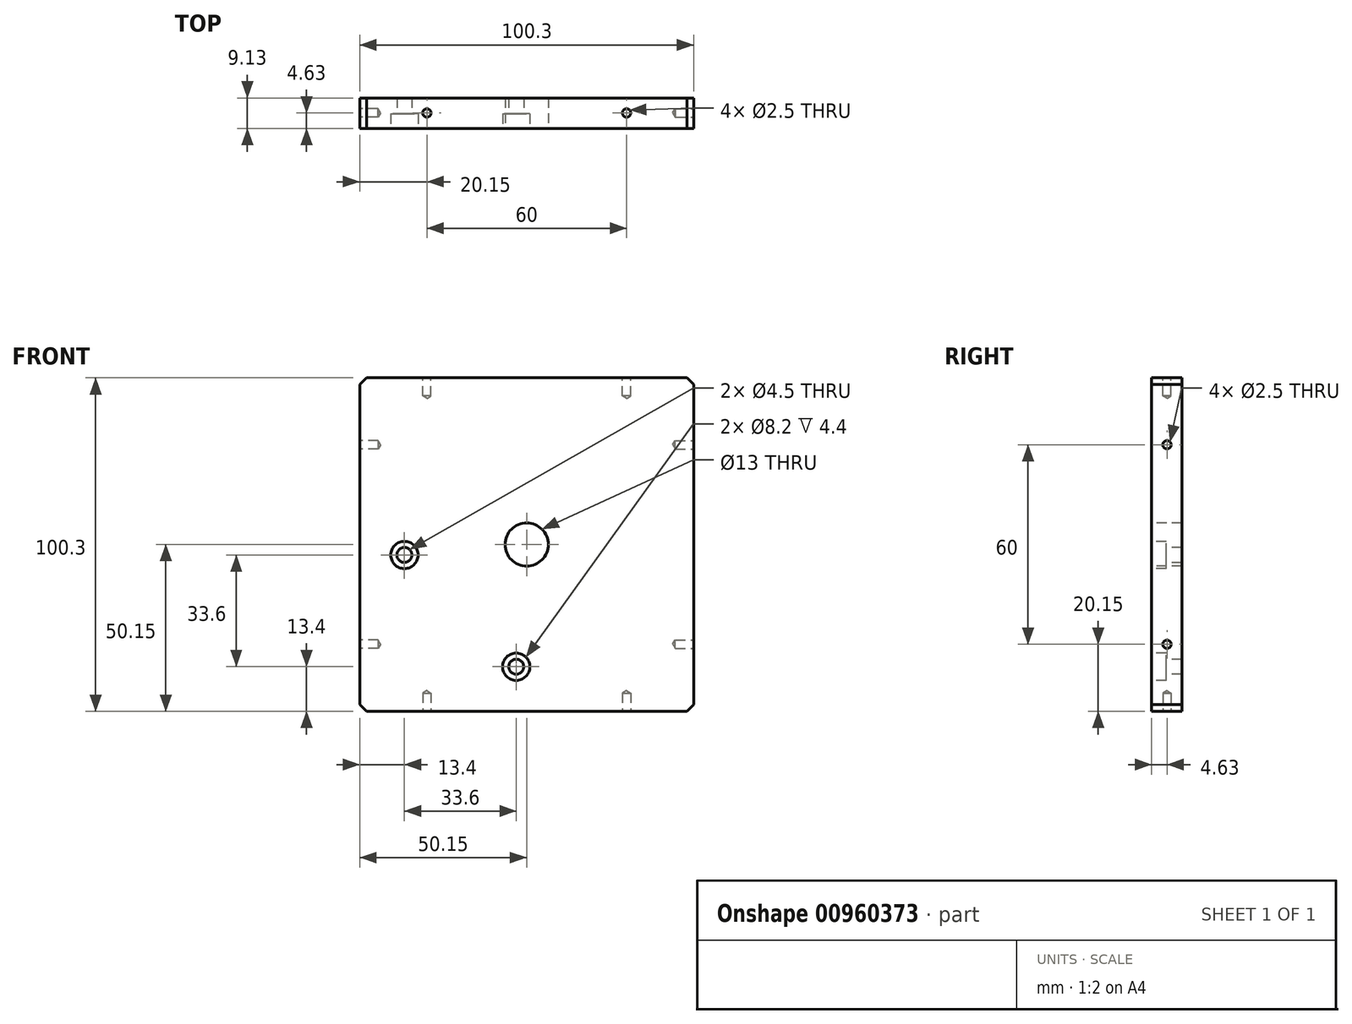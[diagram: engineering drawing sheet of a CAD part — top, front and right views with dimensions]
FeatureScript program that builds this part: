
annotation { "Feature Type Name" : "Feature", "Feature Type Description" : "" }
export const myFeature = defineFeature(function(context is Context, id is Id, definition is map)
    precondition{}
    {
        {
            var Q0;
            Q0=qCreatedBy(makeId("Front.planeOp"),FACE);
            var sketch = newSketch(context, id + "F0", { "sketchPlane" : qUnion([Q0])});
            skLineSegment(sketch, "E0.bottom", {"start": v(50.15, -50.15) * mm, "end": v(-50.15, -50.15) * mm});
            skLineSegment(sketch, "E0.top", {"start": v(50.15, 50.15) * mm, "end": v(-50.15, 50.15) * mm});
            skLineSegment(sketch, "E0.left", {"start": v(50.15, -50.15) * mm, "end": v(50.15, 50.15) * mm});
            skLineSegment(sketch, "E0.right", {"start": v(-50.15, -50.15) * mm, "end": v(-50.15, 50.15) * mm});
            skPoint(sketch, "E0.middle", {"position": v(0, 0) * mm});
            skPoint(sketch, "E1", {"position": v(-37.15, -3.15) * mm});
            skPoint(sketch, "E2", {"position": v(-3.15, -36.75) * mm});
            skSolve(sketch);
        }
        {
            var Q0;
            Q0=makeQuery(id+"F0.imprint","IMPRINT",FACE,{"disambiguationData":[TD([[makeQuery(id+"F0.imprint","IMPRINT",EDGE,{"derivedFrom":sQuery(id+"F0.wireOp",EDGE,"E0.bottom")}),-1.0]])]});
            extrude(context, id + "F1", {"entities" : qUnion([Q0]), "depth" : 9.13 * mm, "offsetDistance" : 25 * mm});
        }
        {
            var Q0;
            Q0=makeQuery(id+"F1.opExtrude","SWEPT_EDGE",EDGE,{"disambiguationData":[OSD([sQuery(id+"F0.wireOp",EDGE,"E0.bottom"),sQuery(id+"F0.wireOp",EDGE,"E0.right")])]});
            var Q1;
            Q1=makeQuery(id+"F1.opExtrude","SWEPT_EDGE",EDGE,{"disambiguationData":[OSD([sQuery(id+"F0.wireOp",EDGE,"E0.bottom"),sQuery(id+"F0.wireOp",EDGE,"E0.left")])]});
            var Q2;
            Q2=makeQuery(id+"F1.opExtrude","SWEPT_EDGE",EDGE,{"disambiguationData":[OSD([sQuery(id+"F0.wireOp",EDGE,"E0.top"),sQuery(id+"F0.wireOp",EDGE,"E0.left")])]});
            var Q3;
            Q3=makeQuery(id+"F1.opExtrude","SWEPT_EDGE",EDGE,{"disambiguationData":[OSD([sQuery(id+"F0.wireOp",EDGE,"E0.top"),sQuery(id+"F0.wireOp",EDGE,"E0.right")])]});
            chamfer(context, id + "F2", {"entities" : qUnion([Q0, Q1, Q2, Q3]), "width" : 2 * mm, "tangentPropagation" : true});
        }
        {
            var Q0;
            Q0=makeQuery(id+"F1.opExtrude","CAP_FACE",FACE,{"disambiguationData":[OSD([sQuery(id+"F0.wireOp",EDGE,"E0.bottom"),sQuery(id+"F0.wireOp",EDGE,"E0.top"),sQuery(id+"F0.wireOp",EDGE,"E0.left"),sQuery(id+"F0.wireOp",EDGE,"E0.right")])],"isStart":false});
            var sketch = newSketch(context, id + "F3", { "sketchPlane" : qUnion([Q0])});
            skPoint(sketch, "E3", {"position": v(-36.75, -3.15) * mm});
            skPoint(sketch, "E4", {"position": v(-3.15, -36.75) * mm});
            skPoint(sketch, "E5", {"position": v(0, 0) * mm});
            skSolve(sketch);
        }
        {
            var Q0;
            Q0=sQuery(id+"F3.wireOp",VERTEX,"E3");
            var Q1;
            Q1=sQuery(id+"F3.wireOp",VERTEX,"E4");
            var Q2;
            Q2=makeQuery(id+"F1.opExtrude","SWEPT_BODY",BODY,{"disambiguationData":[OSD([sQuery(id+"F0.wireOp",EDGE,"E0.bottom"),sQuery(id+"F0.wireOp",EDGE,"E0.top"),sQuery(id+"F0.wireOp",EDGE,"E0.left"),sQuery(id+"F0.wireOp",EDGE,"E0.right")])]});
            hole(context, id + "F4", {"style" : HoleStyle.C_BORE, "endStyle" : HoleEndStyle.THROUGH, "standardTappedOrClearance" : lookupTablePath({ "standard" : "ISO", "size" : "4.5", "type" : "Drilled" }), "standardBlindInLast" : lookupTablePath({ "standard" : "ISO", "size" : "4.5", "type" : "Drilled" }), "holeDiameter" : 4.5 * mm, "cBoreDiameter" : 8.2 * mm, "cBoreDepth" : 4.4 * mm, "majorDiameter" : 5 * mm, "isTappedThrough" : true, "tappedDepth" : 6 * mm, "tapClearance" : 3, "locations" : qUnion([Q0, Q1]), "scope" : qUnion([Q2])});
        }
        {
            var Q0;
            Q0=sQuery(id+"F3.wireOp",VERTEX,"E5");
            var Q1;
            Q1=makeQuery(id+"F1.opExtrude","SWEPT_BODY",BODY,{"disambiguationData":[OSD([sQuery(id+"F0.wireOp",EDGE,"E0.bottom"),sQuery(id+"F0.wireOp",EDGE,"E0.top"),sQuery(id+"F0.wireOp",EDGE,"E0.left"),sQuery(id+"F0.wireOp",EDGE,"E0.right")])]});
            hole(context, id + "F5", {"style" : HoleStyle.SIMPLE, "endStyle" : HoleEndStyle.THROUGH, "standardTappedOrClearance" : lookupTablePath({ "standard" : "ISO", "size" : "13", "type" : "Drilled" }), "standardBlindInLast" : lookupTablePath({ "standard" : "ISO", "size" : "13", "type" : "Drilled" }), "holeDiameter" : 13 * mm, "majorDiameter" : 5 * mm, "isTappedThrough" : true, "tappedDepth" : 6 * mm, "tapClearance" : 3, "locations" : qUnion([Q0]), "scope" : qUnion([Q1])});
        }
        {
            var Q0;
            Q0=makeQuery(id+"F1.opExtrude","SWEPT_FACE",FACE,{"disambiguationData":[OSD([sQuery(id+"F0.wireOp",EDGE,"E0.left")])]});
            var sketch = newSketch(context, id + "F6", { "sketchPlane" : qUnion([Q0])});
            skPoint(sketch, "E6", {"position": v(-4.5, -30) * mm});
            skPoint(sketch, "E7", {"position": v(-4.5, 30) * mm});
            skSolve(sketch);
        }
        {
            var Q0;
            Q0=makeQuery(id+"F1.opExtrude","SWEPT_FACE",FACE,{"disambiguationData":[OSD([sQuery(id+"F0.wireOp",EDGE,"E0.top")])]});
            var sketch = newSketch(context, id + "F7", { "sketchPlane" : qUnion([Q0])});
            skPoint(sketch, "E8", {"position": v(30, -4.5) * mm});
            skPoint(sketch, "E9", {"position": v(-30, -4.5) * mm});
            skSolve(sketch);
        }
        {
            var Q0;
            Q0=makeQuery(id+"F1.opExtrude","SWEPT_FACE",FACE,{"disambiguationData":[OSD([sQuery(id+"F0.wireOp",EDGE,"E0.right")])]});
            var sketch = newSketch(context, id + "F8", { "sketchPlane" : qUnion([Q0])});
            skPoint(sketch, "E10", {"position": v(4.5, 30) * mm});
            skPoint(sketch, "E11", {"position": v(4.5, -30) * mm});
            skSolve(sketch);
        }
        {
            var Q0;
            Q0=makeQuery(id+"F1.opExtrude","SWEPT_FACE",FACE,{"disambiguationData":[OSD([sQuery(id+"F0.wireOp",EDGE,"E0.bottom")])]});
            var sketch = newSketch(context, id + "F9", { "sketchPlane" : qUnion([Q0])});
            skPoint(sketch, "E12", {"position": v(-30, 4.5) * mm});
            skPoint(sketch, "E13", {"position": v(30, 4.5) * mm});
            skSolve(sketch);
        }
        {
            var Q0;
            Q0=sQuery(id+"F8.wireOp",VERTEX,"E11");
            var Q1;
            Q1=sQuery(id+"F8.wireOp",VERTEX,"E10");
            var Q2;
            Q2=sQuery(id+"F7.wireOp",VERTEX,"E9");
            var Q3;
            Q3=sQuery(id+"F7.wireOp",VERTEX,"E8");
            var Q4;
            Q4=sQuery(id+"F6.wireOp",VERTEX,"E6");
            var Q5;
            Q5=sQuery(id+"F6.wireOp",VERTEX,"E7");
            var Q6;
            Q6=sQuery(id+"F9.wireOp",VERTEX,"E13");
            var Q7;
            Q7=sQuery(id+"F9.wireOp",VERTEX,"E12");
            var Q8;
            Q8=makeQuery(id+"F1.opExtrude","SWEPT_BODY",BODY,{"disambiguationData":[OSD([sQuery(id+"F0.wireOp",EDGE,"E0.bottom"),sQuery(id+"F0.wireOp",EDGE,"E0.top"),sQuery(id+"F0.wireOp",EDGE,"E0.left"),sQuery(id+"F0.wireOp",EDGE,"E0.right")])]});
            hole(context, id + "F10", {"style" : HoleStyle.SIMPLE, "endStyle" : HoleEndStyle.BLIND, "standardTappedOrClearance" : lookupTablePath({ "standard" : "ISO", "engagement" : "75%", "pitch" : "0.5 mm", "size" : "M3", "type" : "Tapped" }), "standardBlindInLast" : lookupTablePath({ "standard" : "ISO", "fit" : "Normal", "engagement" : "75%", "pitch" : "0.5 mm", "size" : "M3", "type" : "Clearance & tapped" }), "holeDiameter" : 2.5 * mm, "majorDiameter" : 3 * mm, "showTappedDepth" : true, "holeDepth" : 5.5 * mm, "isTappedThrough" : true, "tappedDepth" : 4 * mm, "tapClearance" : 3, "locations" : qUnion([Q0, Q1, Q2, Q3, Q4, Q5, Q6, Q7]), "scope" : qUnion([Q8])});
        }
    });
